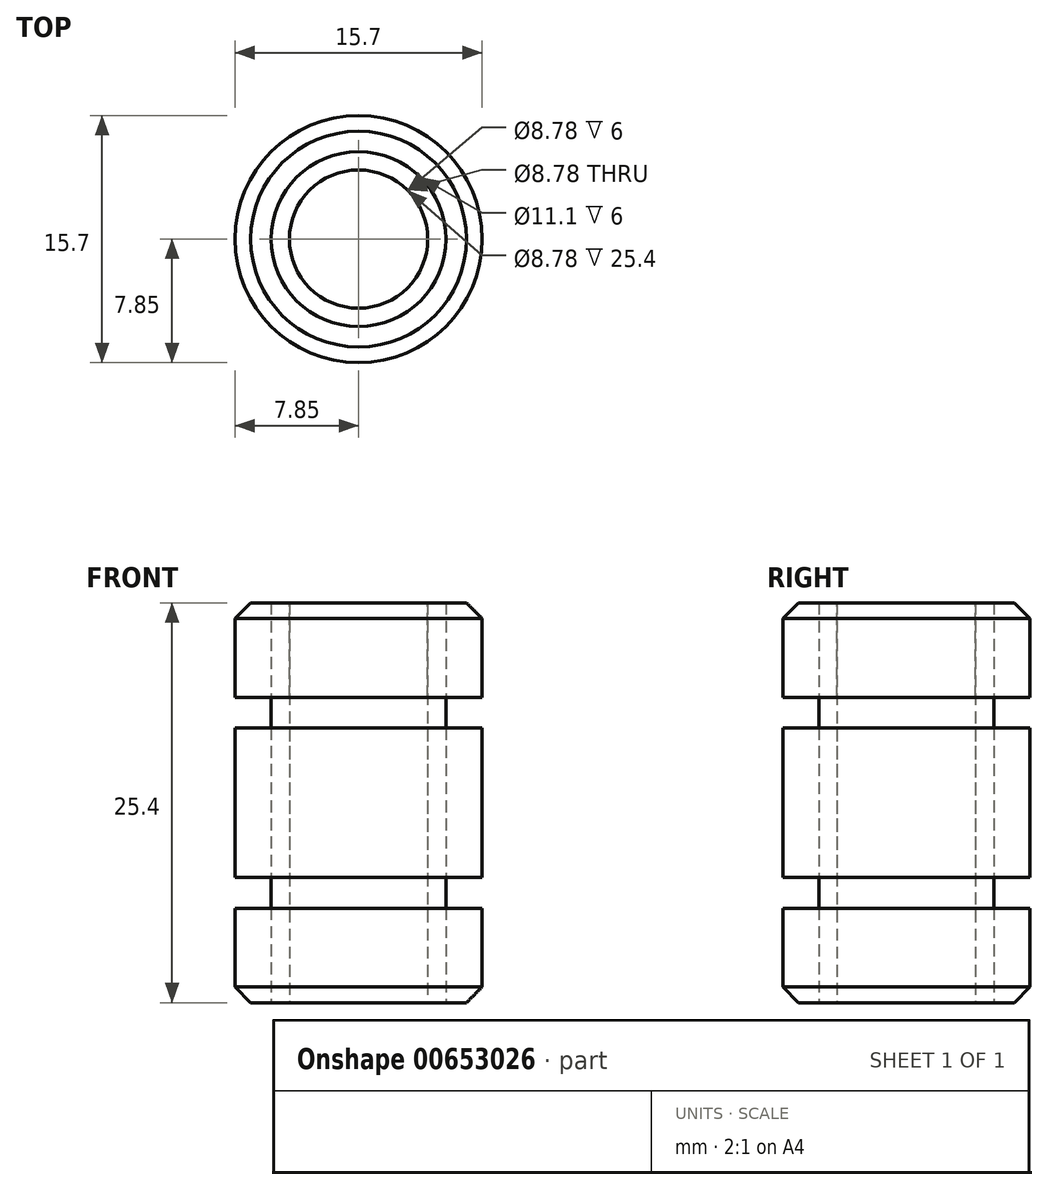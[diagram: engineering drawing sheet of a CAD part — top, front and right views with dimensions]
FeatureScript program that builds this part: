
annotation { "Feature Type Name" : "Feature", "Feature Type Description" : "" }
export const myFeature = defineFeature(function(context is Context, id is Id, definition is map)
    precondition{}
    {
        {
            var Q0;
            Q0=qCreatedBy(makeId("Top.planeOp"),FACE);
            var sketch = newSketch(context, id + "F0", { "sketchPlane" : qUnion([Q0])});
            skCircle(sketch, "E0", {"center": v(0, 0) * mm, "radius": 7.85 * mm});
            skCircle(sketch, "E1", {"center": v(0, 0) * mm, "radius": 4.39 * mm});
            skCircle(sketch, "E2", {"center": v(0, 0) * mm, "radius": 5.55 * mm});
            skSolve(sketch);
        }
        {
            var Q0;
            Q0=makeQuery(id+"F0.imprint","IMPRINT",FACE,{"disambiguationData":[TD([[makeQuery(id+"F0.imprint","IMPRINT",EDGE,{"derivedFrom":sQuery(id+"F0.wireOp",EDGE,"E0")}),1.0]])]});
            extrude(context, id + "F1", {"entities" : qUnion([Q0]), "depth" : 6 * mm, "offsetDistance" : 25 * mm});
        }
        {
            var Q0;
            Q0=makeQuery(id+"F1.opExtrude","CAP_EDGE",EDGE,{"disambiguationData":[OSD([sQuery(id+"F0.wireOp",EDGE,"E0")])],"isStart":true});
            chamfer(context, id + "F2", {"entities" : qUnion([Q0]), "width" : 1 * mm, "tangentPropagation" : true});
        }
        {
            var Q0;
            Q0=sQuery(id+"F0.wireOp",EDGE,"E1");
            extrude(context, id + "F3", {"bodyType" : ToolBodyType.SURFACE, "surfaceEntities" : qUnion([Q0]), "depth" : 25.4 * mm, "offsetDistance" : 25 * mm});
        }
        {
            var Q0;
            Q0=makeQuery(id+"F0.imprint","IMPRINT",FACE,{"disambiguationData":[TD([[makeQuery(id+"F0.imprint","IMPRINT",EDGE,{"derivedFrom":sQuery(id+"F0.wireOp",EDGE,"E1")}),1.0]])]});
            cPlane(context, id + "F4", {"entities" : qUnion([Q0]), "cplaneType" : CPlaneType.OFFSET, "offset" : 25.4 * mm, "width" : 150 * mm, "height" : 150 * mm});
        }
        {
            var Q0;
            Q0=qCreatedBy(id+"F4.planeOp",FACE);
            var sketch = newSketch(context, id + "F5", { "sketchPlane" : qUnion([Q0])});
            skCircle(sketch, "E3", {"center": v(0, 0) * mm, "radius": 7.85 * mm});
            skCircle(sketch, "E4", {"center": v(0, 0) * mm, "radius": 4.39 * mm});
            skSolve(sketch);
        }
        {
            var Q0;
            Q0 = qSketchRegion(id + "F5", true);
            extrude(context, id + "F6", {"entities" : qUnion([Q0]), "depth" : -6 * mm, "offsetDistance" : 25 * mm});
        }
        {
            var Q0;
            Q0=makeQuery(id+"F6.opExtrude","CAP_EDGE",EDGE,{"disambiguationData":[OSD([sQuery(id+"F5.wireOp",EDGE,"E3")])],"isStart":true});
            chamfer(context, id + "F7", {"entities" : qUnion([Q0]), "width" : 1 * mm, "tangentPropagation" : true});
        }
        {
            var Q0;
            Q0=makeQuery(id+"F0.imprint","IMPRINT",FACE,{"disambiguationData":[TD([[makeQuery(id+"F0.imprint","IMPRINT",EDGE,{"derivedFrom":sQuery(id+"F0.wireOp",EDGE,"E1")}),-1.0]])]});
            extrude(context, id + "F8", {"entities" : qUnion([Q0]), "depth" : 25.4 * mm, "offsetDistance" : 25 * mm});
        }
        {
            var Q0;
            Q0=qCreatedBy(makeId("Top.planeOp"),FACE);
            cPlane(context, id + "F9", {"entities" : qUnion([Q0]), "cplaneType" : CPlaneType.OFFSET, "offset" : 12.7 * mm, "width" : 150 * mm, "height" : 150 * mm});
        }
        {
            var Q0;
            Q0=qCreatedBy(id+"F9.planeOp",FACE);
            var sketch = newSketch(context, id + "F10", { "sketchPlane" : qUnion([Q0])});
            skCircle(sketch, "E5", {"center": v(0, 0) * mm, "radius": 7.85 * mm});
            skCircle(sketch, "E6", {"center": v(0, 0) * mm, "radius": 4.39 * mm});
            skSolve(sketch);
        }
        {
            var Q0;
            Q0 = qSketchRegion(id + "F10", true);
            extrude(context, id + "F11", {"entities" : qUnion([Q0]), "endBound" : BoundingType.SYMMETRIC, "depth" : 9.5 * mm, "offsetDistance" : 25 * mm});
        }
    });
